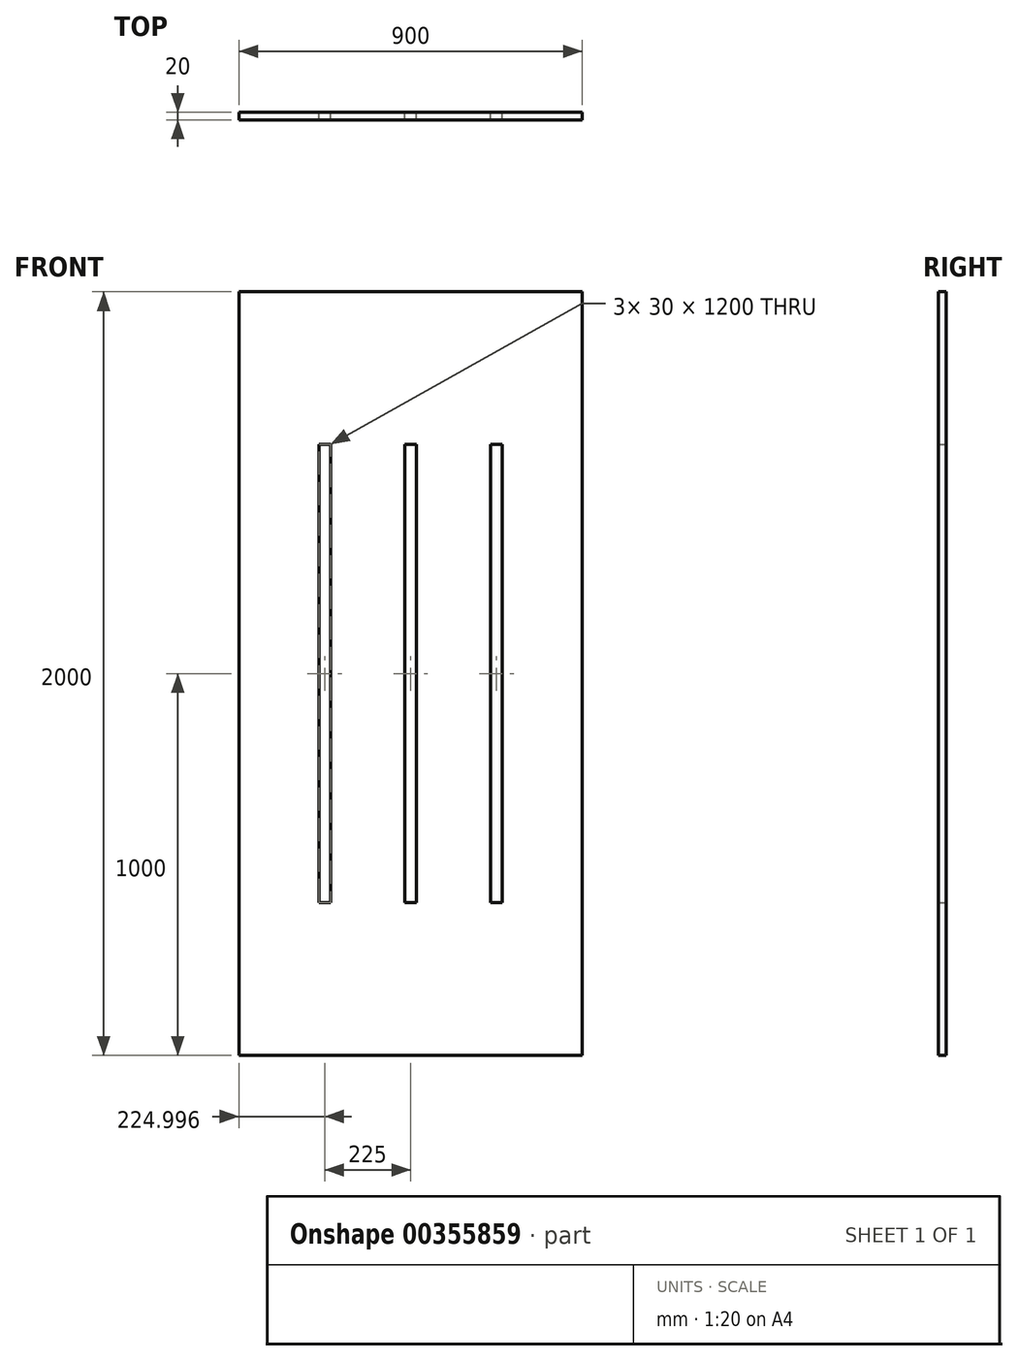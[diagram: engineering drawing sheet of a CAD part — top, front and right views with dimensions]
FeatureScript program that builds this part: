
annotation { "Feature Type Name" : "Feature", "Feature Type Description" : "" }
export const myFeature = defineFeature(function(context is Context, id is Id, definition is map)
    precondition{}
    {
        {
            var Q0;
            Q0=qCreatedBy(makeId("Front.planeOp"),FACE);
            var sketch = newSketch(context, id + "F0", { "sketchPlane" : qUnion([Q0])});
            skLineSegment(sketch, "E0.bottom", {"start": v(-70.66, 2542) * mm, "end": v(829.34, 2542) * mm});
            skLineSegment(sketch, "E0.top", {"start": v(-70.66, 542) * mm, "end": v(829.34, 542) * mm});
            skLineSegment(sketch, "E0.left", {"start": v(-70.66, 2542) * mm, "end": v(-70.66, 542) * mm});
            skLineSegment(sketch, "E0.right", {"start": v(829.34, 2542) * mm, "end": v(829.34, 542) * mm});
            skLineSegment(sketch, "E1", {"start": v(154.34, 2142) * mm, "end": v(169.34, 2142) * mm});
            skPoint(sketch, "E2.start.orphan", {"position": v(379.34, 2542) * mm});
            skPoint(sketch, "E3.orphan", {"position": v(-70.66, 2142) * mm});
            skLineSegment(sketch, "E4.0", {"start": v(139.34, 2142) * mm, "end": v(139.34, 942) * mm});
            skLineSegment(sketch, "E5.MirrorCS", {"start": v(169.34, 2142) * mm, "end": v(169.34, 942) * mm});
            skLineSegment(sketch, "E6.0", {"start": v(364.34, 2142) * mm, "end": v(364.34, 1842) * mm});
            skLineSegment(sketch, "E7.MirrorCS", {"start": v(619.34, 1342) * mm, "end": v(619.34, 1042) * mm});
            skLineSegment(sketch, "E8", {"start": v(139.34, 942) * mm, "end": v(169.34, 942) * mm});
            skPoint(sketch, "E9.end.orphan", {"position": v(154.34, 1042) * mm});
            skLineSegment(sketch, "E10.trimOffspring", {"start": v(364.34, 2142) * mm, "end": v(379.34, 2142) * mm});
            skLineSegment(sketch, "E11", {"start": v(139.34, 2142) * mm, "end": v(154.34, 2142) * mm});
            skLineSegment(sketch, "E12", {"start": v(364.34, 1842) * mm, "end": v(364.34, 942) * mm});
            skLineSegment(sketch, "E13", {"start": v(364.34, 942) * mm, "end": v(394.34, 942) * mm});
            skPoint(sketch, "E14.endSnap0", {"position": v(379.34, 942) * mm});
            skLineSegment(sketch, "E15", {"start": v(589.34, 942) * mm, "end": v(619.34, 942) * mm});
            skLineSegment(sketch, "E16", {"start": v(619.34, 942) * mm, "end": v(619.34, 1042) * mm});
            skPoint(sketch, "E17.end.orphan", {"position": v(394.34, 1042) * mm});
            skLineSegment(sketch, "E18", {"start": v(394.34, 1342) * mm, "end": v(394.34, 942) * mm});
            skLineSegment(sketch, "E19", {"start": v(589.34, 942) * mm, "end": v(589.34, 1342) * mm});
            skLineSegment(sketch, "E20.top", {"start": v(619.34, 2142) * mm, "end": v(589.34, 2142) * mm});
            skLineSegment(sketch, "E20.left", {"start": v(619.34, 1342) * mm, "end": v(619.34, 2142) * mm});
            skLineSegment(sketch, "E20.right", {"start": v(589.34, 1342) * mm, "end": v(589.34, 2142) * mm});
            skLineSegment(sketch, "E21", {"start": v(394.34, 1342) * mm, "end": v(394.34, 2142) * mm});
            skLineSegment(sketch, "E22", {"start": v(394.34, 2142) * mm, "end": v(379.34, 2142) * mm});
            skPoint(sketch, "E23.MirrorCS.start.orphan", {"position": v(604.34, 1342) * mm});
            skSolve(sketch);
        }
        {
            var Q0;
            Q0=makeQuery(id+"F0.imprint","IMPRINT",FACE,{"disambiguationData":[TD([[makeQuery(id+"F0.imprint","IMPRINT",EDGE,{"derivedFrom":sQuery(id+"F0.wireOp",EDGE,"E0.bottom")}),-1.0]])]});
            extrude(context, id + "F1", {"entities" : qUnion([Q0]), "depth" : 20 * mm});
        }
    });
